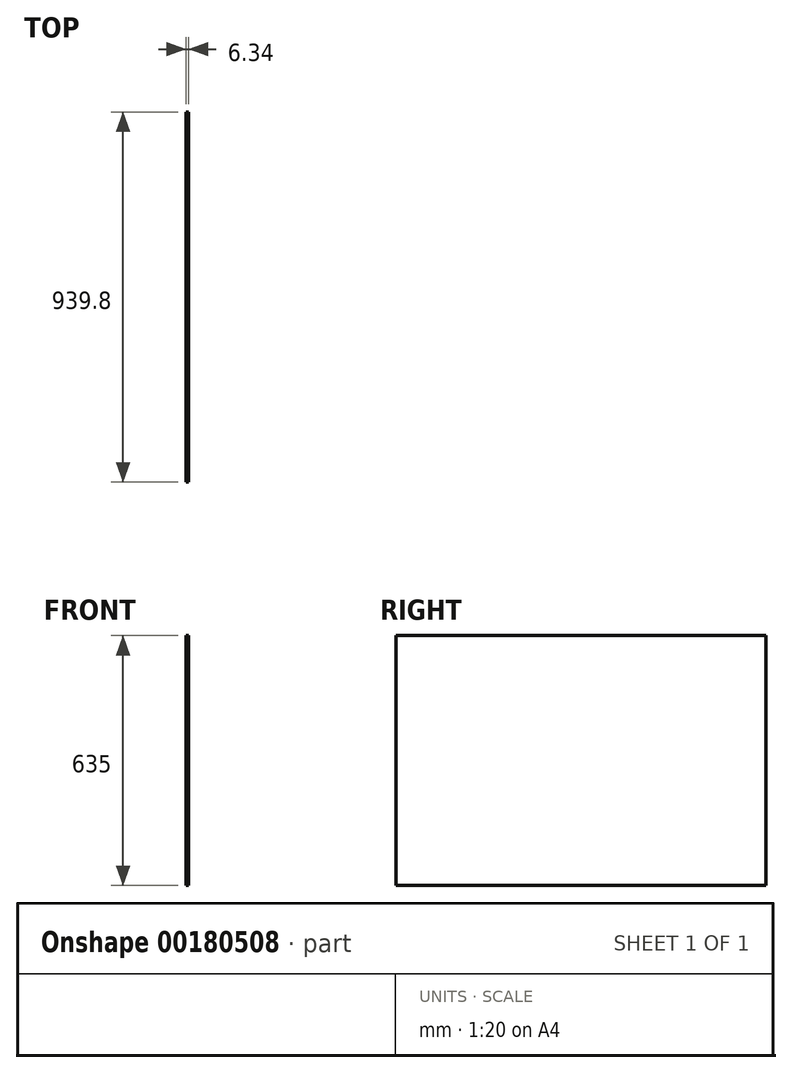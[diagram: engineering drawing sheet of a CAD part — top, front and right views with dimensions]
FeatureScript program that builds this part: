
annotation { "Feature Type Name" : "Feature", "Feature Type Description" : "" }
export const myFeature = defineFeature(function(context is Context, id is Id, definition is map)
    precondition{}
    {
        {
            var Q0;
            Q0=qCreatedBy(makeId("Right.planeOp"),FACE);
            var sketch = newSketch(context, id + "F0", { "sketchPlane" : qUnion([Q0])});
            skLineSegment(sketch, "E0.bottom", {"start": v(469.9, 317.5) * mm, "end": v(-469.9, 317.5) * mm});
            skLineSegment(sketch, "E0.top", {"start": v(469.9, -317.5) * mm, "end": v(-469.9, -317.5) * mm});
            skLineSegment(sketch, "E0.left", {"start": v(469.9, 317.5) * mm, "end": v(469.9, -317.5) * mm});
            skLineSegment(sketch, "E0.right", {"start": v(-469.9, 317.5) * mm, "end": v(-469.9, -317.5) * mm});
            skPoint(sketch, "E0.middle", {"position": v(0, 0) * mm});
            skSolve(sketch);
        }
        {
            var Q0;
            Q0 = qSketchRegion(id + "F0", true);
            extrude(context, id + "F1", {"entities" : qUnion([Q0]), "endBound" : BoundingType.SYMMETRIC, "depth" : 6.35 * mm});
        }
    });
